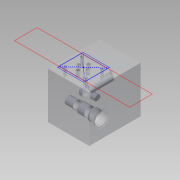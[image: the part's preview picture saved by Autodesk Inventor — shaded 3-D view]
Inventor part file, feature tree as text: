
AUTODESK INVENTOR PART (.ipt)
format: ipt  version: 2014 (Build 180170000, 170)  size: 419,328 bytes
history: native  units: mm
features: other x63, sketch x14, extrude x1
ambient origin geometry x8: Origin, YZ Plane, XZ Plane, XY Plane, X Axis, Y Axis, Z Axis, Center Point
bodies: 实体1 (feature_tree)
feature tree (78):
  other  "NULLNET"
  extrude  "拉伸1"  TaperAngle=0.0deg  [1 undecoded]
  other  "UCS1"
  other  "UCS2"
  other  "UCS3"
  other  "UCS4"
  other  "UCS5"
  other  "UCS6"
  other  "Footprint1"
  other  "Outline1"
  sketch  "草图1"  dims[d0=90.0mm d1=0.0mm]
  sketch  "草图5"  dims[d14=0.0mm d15=0.0mm d16=0.0mm d17=0.0mm d18=0.0mm d19=0.0mm]
  other  "曲面1"
  sketch  "草图6"  dims[d20=0.0mm d21=0.0mm d22=0.0mm d23=0.0mm d24=0.0mm d25=0.0mm]
  other  "曲面2"
  sketch  "草图7"  dims[d26=0.0mm d27=0.0mm d28=0.0mm d29=0.0mm d30=0.0mm d31=0.0mm]
  other  "曲面3"
  sketch  "草图8"  dims[d32=0.0mm d33=0.0mm d34=0.0mm d35=0.0mm d36=0.0mm d37=0.0mm d38=0.0mm]
  other  "曲面4"
  sketch  "草图10"  dims[d56=-48.42mm]
  other  "曲面5"
  sketch  "草图11"  dims[d57=15.87mm d58=0.0mm]
  other  "曲面6"
  sketch  "草图12"  dims[d59=0.13mm d60=-10.297443mm]
  other  "曲面7"
  sketch  "草图14"  dims[d62=13.5mm d63=0.0mm]
  other  "曲面8"
  sketch  "草图15"  dims[d64=-14.359mm d65=3.18mm d66=0.0mm d67=0.0mm d71=-30.09mm d72=8.8mm d73=0.0mm d74=0.13mm d75=-10.297443mm d76=-14.359mm d77=6.35mm d78=0.0mm d79=0.0mm d83=-13.99mm d84=38.81mm d85=0.0mm d86=0.13mm d87=-10.297443mm]
  other  "曲面9"
  other  "2-1cone"
  other  "3-1cone"
  other  "4-1cone"
  other  "UCS1: YZ 平面"
  other  "UCS1: XZ 平面"
  other  "UCS1: XY 平面"
  other  "UCS1: X 轴"
  other  "UCS1: Y 轴"
  other  "UCS1: Z 轴"
  other  "UCS1: 原点"
  other  "UCS2: YZ 平面"
  other  "UCS2: XZ 平面"
  other  "UCS2: XY 平面"
  other  "UCS2: X 轴"
  other  "UCS2: Y 轴"
  other  "UCS2: Z 轴"
  other  "UCS2: 原点"
  other  "UCS3: YZ 平面"
  other  "UCS3: XZ 平面"
  other  "UCS3: XY 平面"
  other  "UCS3: X 轴"
  other  "UCS3: Y 轴"
  other  "UCS3: Z 轴"
  other  "UCS3: 原点"
  other  "UCS4: YZ 平面"
  other  "UCS4: XZ 平面"
  other  "UCS4: XY 平面"
  other  "UCS4: X 轴"
  other  "UCS4: Y 轴"
  other  "UCS4: Z 轴"
  other  "UCS4: 原点"
  other  "UCS5: YZ 平面"
  other  "UCS5: XZ 平面"
  other  "UCS5: XY 平面"
  other  "UCS5: X 轴"
  other  "UCS5: Y 轴"
  other  "UCS5: Z 轴"
  other  "UCS5: 原点"
  other  "UCS6: YZ 平面"
  other  "UCS6: XZ 平面"
  other  "UCS6: XY 平面"
  other  "UCS6: X 轴"
  other  "UCS6: Y 轴"
  other  "UCS6: Z 轴"
  other  "UCS6: 原点"
  sketch  "草图2"  dims[d2=0.0mm d3=0.0mm d4=0.0mm d5=0.0mm d6=0.0mm d7=0.0mm]
  sketch  "草图4"  dims[d8=0.0mm d9=0.0mm d10=0.0mm d11=0.0mm d12=0.0mm d13=0.0mm]
  sketch  "草图9"  dims[d52=0.0mm]
  sketch  "草图13"  dims[d61=-31.039mm]
note: 1 required parameter value undecoded (feature->parameter linkage not recoverable at this tier; creation-order binding heuristic only, values carry confidence <= 0.55)
